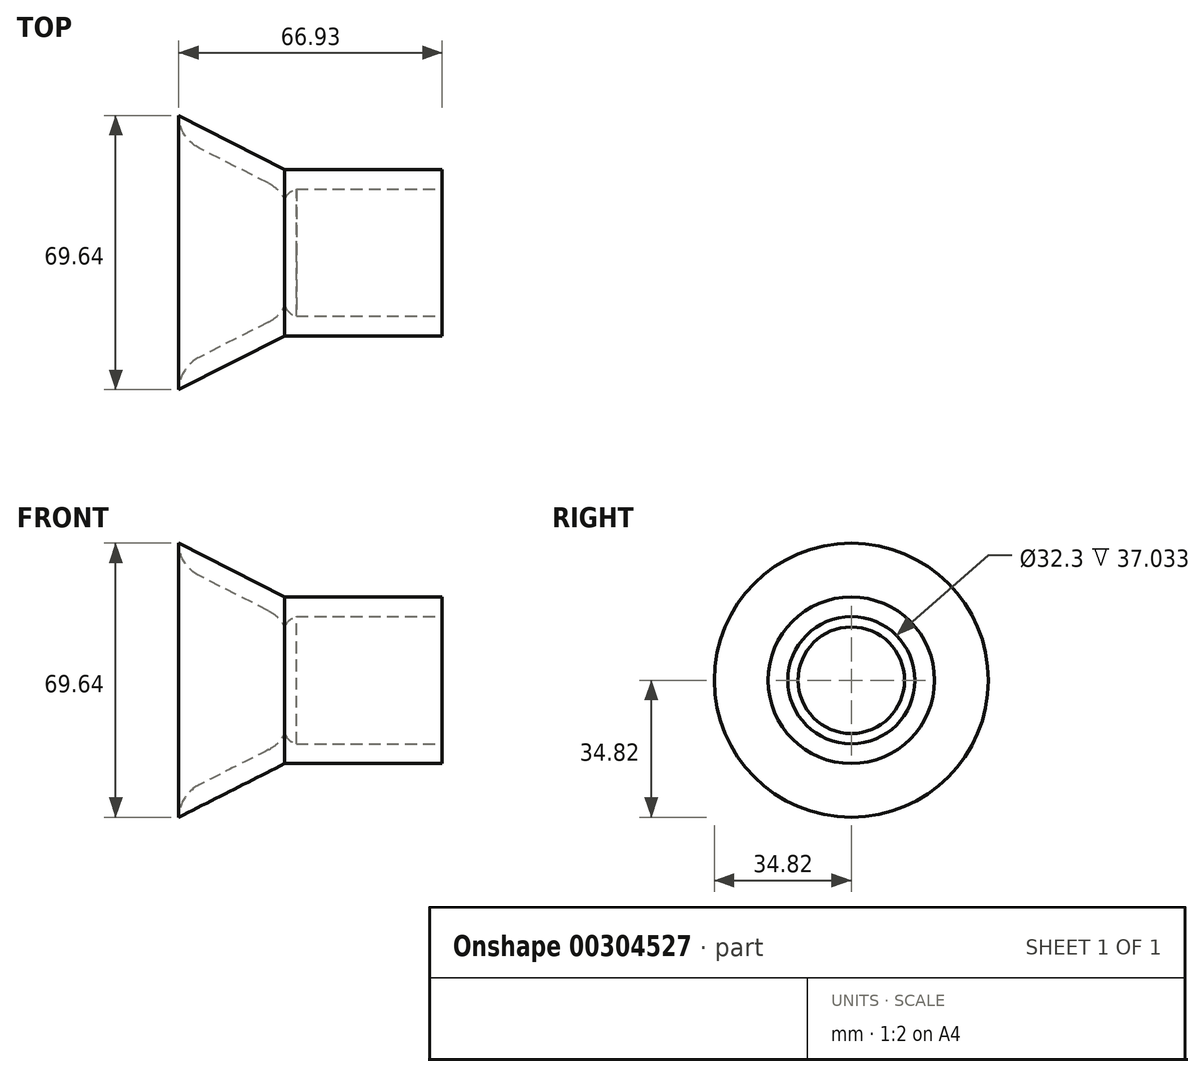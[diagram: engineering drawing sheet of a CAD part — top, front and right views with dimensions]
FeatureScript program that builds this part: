
annotation { "Feature Type Name" : "Feature", "Feature Type Description" : "" }
export const myFeature = defineFeature(function(context is Context, id is Id, definition is map)
    precondition{}
    {
        {
            var Q0;
            Q0=qCreatedBy(makeId("Front.planeOp"),FACE);
            var sketch = newSketch(context, id + "F0", { "sketchPlane" : qUnion([Q0])});
            skLineSegment(sketch, "E0", {"start": v(0, 0) * mm, "end": v(-53.91, 0) * mm, "construction": true});
            skLineSegment(sketch, "E1", {"start": v(0, 0) * mm, "end": v(53.36, 0) * mm, "construction": true});
            skLineSegment(sketch, "E2", {"start": v(40, 16.15) * mm, "end": v(0, 16.15) * mm});
            skLineSegment(sketch, "E3", {"start": v(40, 16.15) * mm, "end": v(40, 21.15) * mm});
            skLineSegment(sketch, "E4", {"start": v(40, 21.15) * mm, "end": v(0, 21.15) * mm});
            skLineSegment(sketch, "E5", {"start": v(0, 16.15) * mm, "end": v(0, 13.53) * mm});
            skLineSegment(sketch, "E6", {"start": v(0, 13.53) * mm, "end": v(-1, 13.53) * mm});
            skLineSegment(sketch, "E7", {"start": v(0, 21.15) * mm, "end": v(-26.93, 34.82) * mm});
            skArc(sketch, "E8", {"start": v(2.97, 16.15) * mm, "mid": v(1.16, 15.2) * mm, "end": v(0, 13.53) * mm});
            skLineSegment(sketch, "E9", {"start": v(-4.1, 17.63) * mm, "end": v(-21.75, 26.58) * mm});
            skArc(sketch, "E10", {"start": v(0, 13.53) * mm, "mid": v(-1.73, 15.9) * mm, "end": v(-4.1, 17.63) * mm});
            skArc(sketch, "E11", {"start": v(-26.93, 34.82) * mm, "mid": v(-25.48, 29.98) * mm, "end": v(-21.75, 26.58) * mm});
            skSolve(sketch);
        }
        {
            var Q0;
            Q0=makeQuery(id+"F0.imprint","IMPRINT",FACE,{"disambiguationData":[TD([[makeQuery(id+"F0.imprint","IMPRINT",EDGE,{"derivedFrom":sQuery(id+"F0.wireOp",EDGE,"E2")}),-1.0]])]});
            var Q1;
            {var subQ0=sQuery(id+"F0.wireOp",EDGE,"E5");Q1=makeQuery(id+"F0.imprint","IMPRINT",FACE,{"disambiguationData":[TD([[makeQuery(id+"F0.imprint","IMPRINT",EDGE,{"derivedFrom":subQ0}),1.0]])]});}
            var Q2;
            Q2=sQuery(id+"F0.wireOp",EDGE,"E0");
            revolve(context, id + "F1", {"entities" : qUnion([Q0, Q1]), "axis" : qUnion([Q2]), "revolveType" : RevolveType.FULL});
        }
    });
